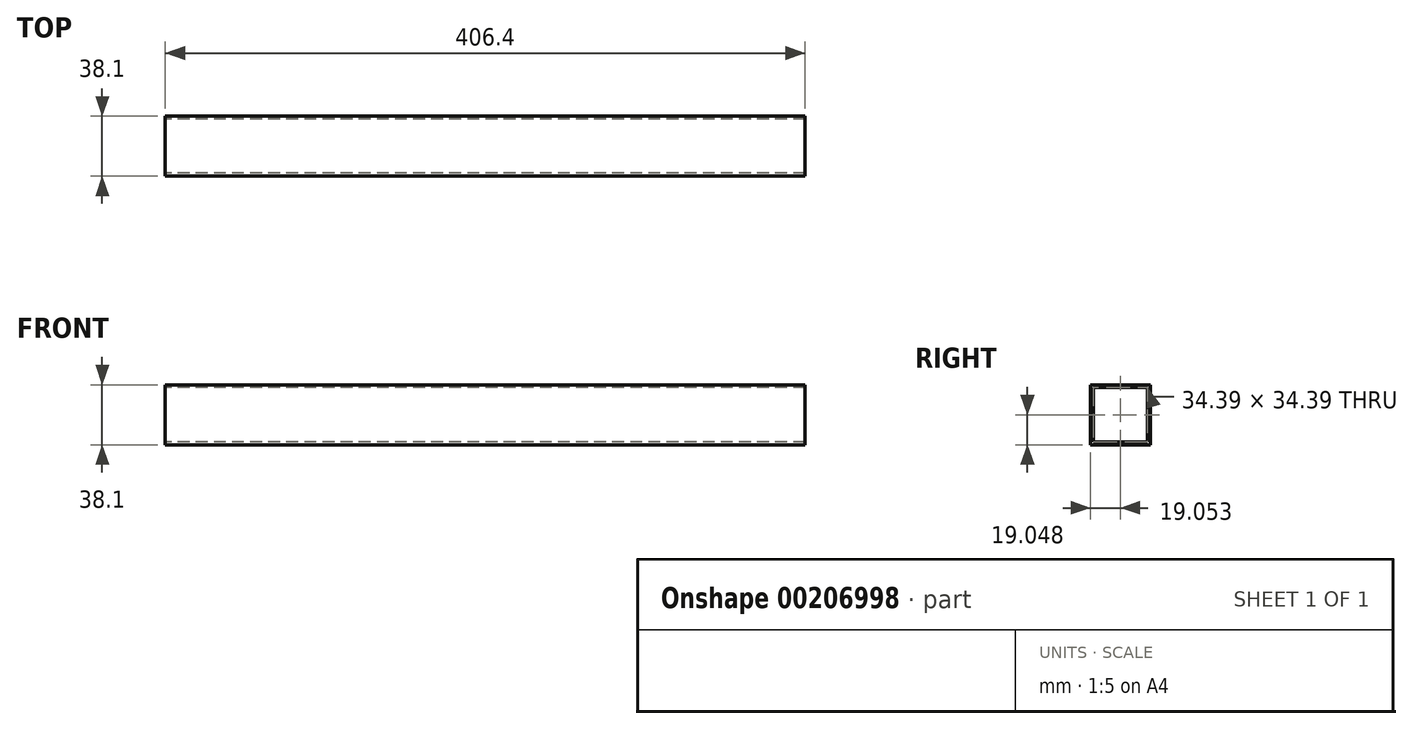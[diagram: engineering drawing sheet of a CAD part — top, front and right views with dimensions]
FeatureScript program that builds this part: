
annotation { "Feature Type Name" : "Feature", "Feature Type Description" : "" }
export const myFeature = defineFeature(function(context is Context, id is Id, definition is map)
    precondition{}
    {
        {
            var Q0;
            Q0=qCreatedBy(makeId("Right.planeOp"),FACE);
            var sketch = newSketch(context, id + "F0", { "sketchPlane" : qUnion([Q0])});
            skLineSegment(sketch, "E0.bottom", {"start": v(-10, -21.42) * mm, "end": v(28.1, -21.42) * mm});
            skLineSegment(sketch, "E0.top", {"start": v(-10, 16.68) * mm, "end": v(28.1, 16.68) * mm});
            skLineSegment(sketch, "E0.left", {"start": v(-10, -21.42) * mm, "end": v(-10, 16.68) * mm});
            skLineSegment(sketch, "E0.right", {"start": v(28.1, -21.42) * mm, "end": v(28.1, 16.68) * mm});
            skLineSegment(sketch, "E1.bottom", {"start": v(-8.15, -19.57) * mm, "end": v(26.24, -19.57) * mm});
            skLineSegment(sketch, "E1.top", {"start": v(-8.15, 14.82) * mm, "end": v(26.24, 14.82) * mm});
            skLineSegment(sketch, "E1.left", {"start": v(-8.15, -19.57) * mm, "end": v(-8.15, 14.82) * mm});
            skLineSegment(sketch, "E1.right", {"start": v(26.24, -19.57) * mm, "end": v(26.24, 14.82) * mm});
            skSolve(sketch);
        }
        {
            var Q0;
            Q0 = qSketchRegion(id + "F0", true);
            extrude(context, id + "F1", {"entities" : qUnion([Q0]), "depth" : 406.4 * mm});
        }
    });
